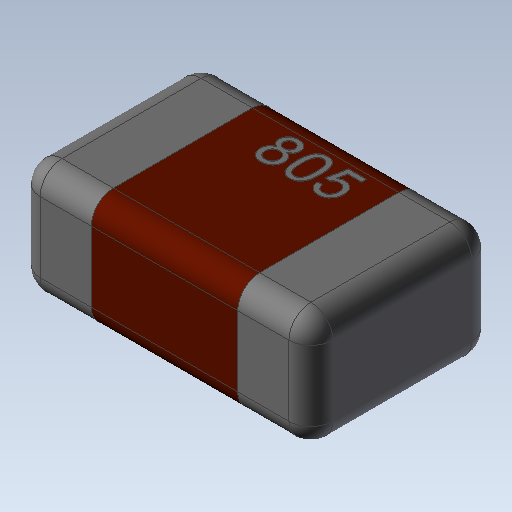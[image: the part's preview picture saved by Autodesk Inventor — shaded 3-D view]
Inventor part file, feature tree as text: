
AUTODESK INVENTOR PART (.ipt)
format: ipt  version: 2020 (Build 240168000, 168)  size: 277,504 bytes
history: native  units: in
note: dims shown in document units (in); Inventor stores cm internally (conversion verified against a paired STEP export)
features: extrude x1
ambient origin geometry x8: Origin, YZ Plane, XZ Plane, XY Plane, X Axis, Y Axis, Z Axis, Center Point
bodies: Solid1 (feature_tree)
feature tree (1):
  extrude  "Extrude2"  [1 undecoded]
note: 1 required parameter value undecoded (feature->parameter linkage not recoverable at this tier; creation-order binding heuristic only, values carry confidence <= 0.55)
